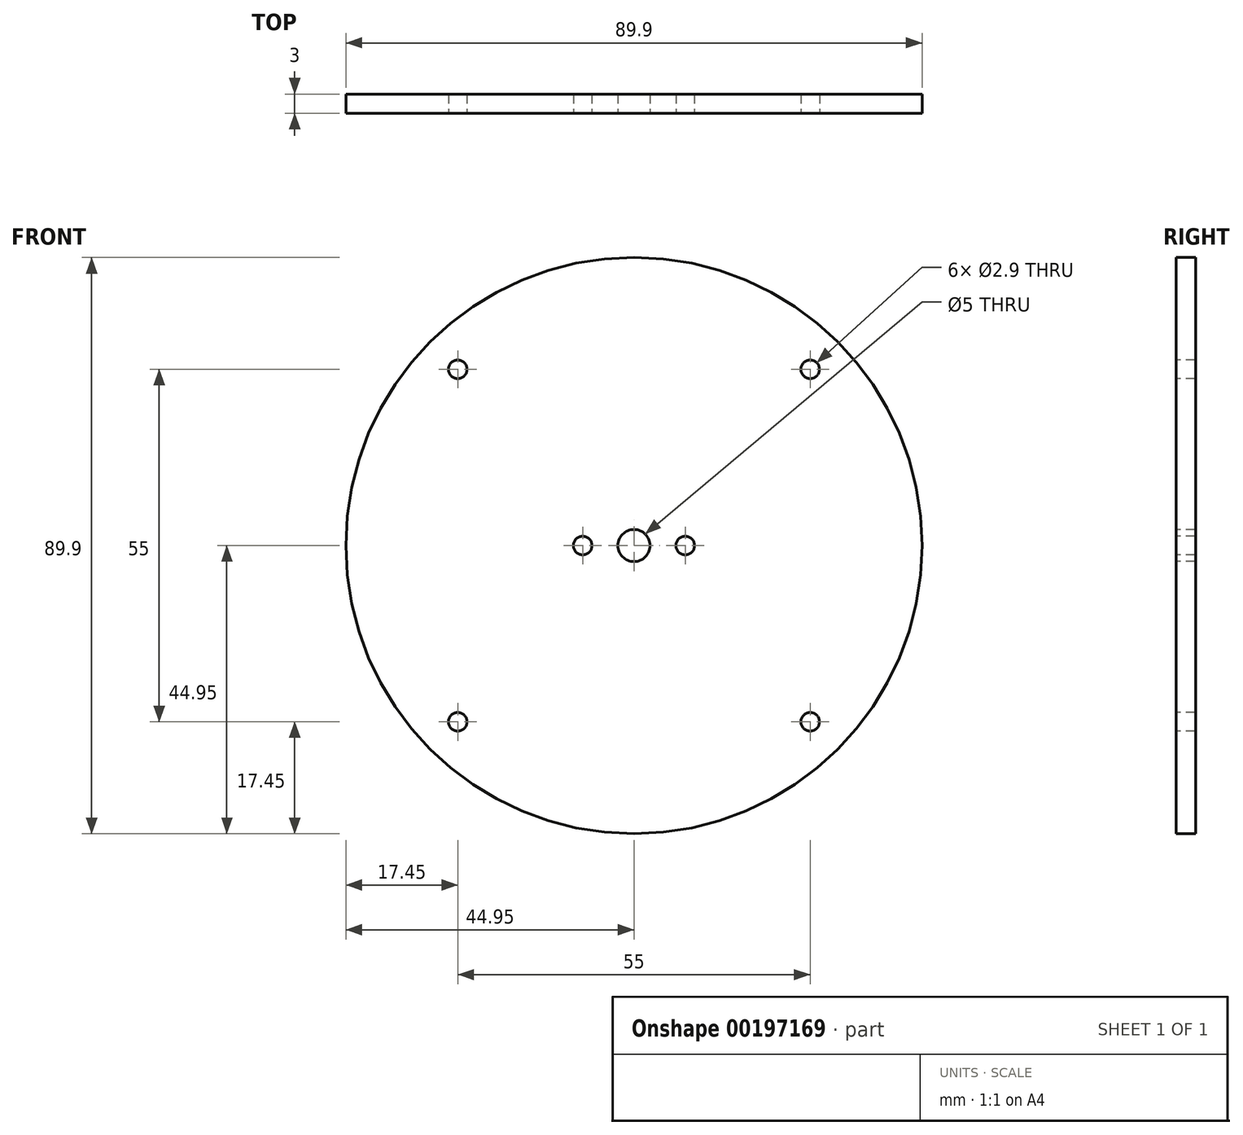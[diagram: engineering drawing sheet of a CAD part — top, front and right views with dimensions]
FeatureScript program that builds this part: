
annotation { "Feature Type Name" : "Feature", "Feature Type Description" : "" }
export const myFeature = defineFeature(function(context is Context, id is Id, definition is map)
    precondition{}
    {
        {
            var Q0;
            Q0=qCreatedBy(makeId("Front.planeOp"),FACE);
            var sketch = newSketch(context, id + "F0", { "sketchPlane" : qUnion([Q0])});
            skCircle(sketch, "E0", {"center": v(0, 0) * mm, "radius": 44.95 * mm});
            skSolve(sketch);
        }
        {
            var Q0;
            Q0 = qSketchRegion(id + "F0", true);
            extrude(context, id + "F1", {"entities" : qUnion([Q0]), "depth" : 3 * mm});
        }
        {
            var Q0;
            Q0=makeQuery(id+"F1.opExtrude","CAP_FACE",FACE,{"disambiguationData":[OSD([sQuery(id+"F0.wireOp",EDGE,"E0")])],"isStart":false});
            var sketch = newSketch(context, id + "F2", { "sketchPlane" : qUnion([Q0])});
            skLineSegment(sketch, "E1", {"start": v(-44.95, 0) * mm, "end": v(44.95, 0) * mm, "construction": true});
            skLineSegment(sketch, "E2", {"start": v(0, 0) * mm, "end": v(0, 33.83) * mm, "construction": true});
            skCircle(sketch, "E3", {"center": v(-8, 0) * mm, "radius": 1.45 * mm});
            skCircle(sketch, "E4.MirrorC", {"center": v(8, 0) * mm, "radius": 1.45 * mm});
            skCircle(sketch, "E5", {"center": v(0, 0) * mm, "radius": 2.5 * mm});
            skSolve(sketch);
        }
        {
            var Q0;
            Q0 = qSketchRegion(id + "F2", true);
            extrude(context, id + "F3", {"entities" : qUnion([Q0]), "operationType" : NewBodyOperationType.REMOVE, "endBound" : BoundingType.THROUGH_ALL, "oppositeDirection" : true, "depth" : 25 * mm});
        }
        {
            var Q0;
            Q0=makeQuery(id+"F1.opExtrude","CAP_FACE",FACE,{"disambiguationData":[OSD([sQuery(id+"F0.wireOp",EDGE,"E0")])],"isStart":false});
            var sketch = newSketch(context, id + "F4", { "sketchPlane" : qUnion([Q0])});
            skLineSegment(sketch, "E6", {"start": v(0, 0) * mm, "end": v(0, 23.9) * mm, "construction": true});
            skLineSegment(sketch, "E7", {"start": v(0, 0) * mm, "end": v(-31.3, 0) * mm, "construction": true});
            skCircle(sketch, "E8", {"center": v(-27.5, 27.5) * mm, "radius": 1.45 * mm});
            skCircle(sketch, "E9.MirrorC", {"center": v(27.5, 27.5) * mm, "radius": 1.45 * mm});
            skCircle(sketch, "E10.MirrorC", {"center": v(-27.5, -27.5) * mm, "radius": 1.45 * mm});
            skCircle(sketch, "E11.MirrorC", {"center": v(27.5, -27.5) * mm, "radius": 1.45 * mm});
            skSolve(sketch);
        }
        {
            var Q0;
            Q0 = qSketchRegion(id + "F4", true);
            extrude(context, id + "F5", {"entities" : qUnion([Q0]), "operationType" : NewBodyOperationType.REMOVE, "endBound" : BoundingType.THROUGH_ALL, "oppositeDirection" : true, "depth" : 25 * mm});
        }
    });
